# Revit family: LAMP_FIL 70 TECH RECESSED
name_source: partatom
category: Luminarias
revit_build: Autodesk Revit 2015 (Build: 20140606_1530(x64)
units: mm (PartAtom-declared; Revit-internal decimal feet)

## types (16) — shared parameters
CRI = 80
Cambio de temperatura de color de luz atenuada = <Ninguno>
Comentarios de tipo = Availability of switching between accessories through visibility parameters when placed in a project.
Fabricante = LAMP
Filtro de color = 16777215
Gear = Electronic
IEE = A+
IFC Clasificación = Light Fixture
Installation instructions = https://www.lamp.es
Insulation class = I
LED Lifetime = 50.000 L80 B10
Last update = 17/08/2020
Luminaire type = Indoor - Modular System
Lámpara = LED MID-POWER
MacAdam = 3
Manufacturer URL = http://www.lamp.es
Manufacturer country = Spain
Manufacturer name = LAMP
Material Reflector = LAMP_PC Reflector Fil Tech Metalizado
Model explanation = Availability of switching between accessories through visibility parameters when placed in a project.
Product URL = https://www.lamp.es
Product datasheet = https://www.lamp.es
Protection rating = IP20
Type = MID POWER NICHIA
UGR = 19
Ángulo de inclinación = 90,00°

## per-type parameters (varying)
| type | Archivo de red fotométrica | Descripción | Dimensions | Efficacy | Finish | Longitud | Longitud de línea de emisión | Material Perfil | Modelo | Plum | Power | Power Supply | Product code | Recessed dimensions | UniClass 1.4 Code | UniClass 2.0 Code | Weight |
| 1000MM 1600LM 3000K WHITE | 4741120.IES | FIL 70 TECH REC 1M 1600 WW WH. | 1000 x 70 x 70 mm | 106 lm/W | Matt white | 1000 mm  [stored 3.28084 ft] | 1000 mm  [stored 3.28084 ft] | LAMP_Aluminio Perfil Fil BL | F71RE100LOTS830NW | 15 W | 12 W | 230V-50Hz | F71RE100LOTS830NW | 1012 x 78 x 85 mm | F71RE100LOTS830NW | F71RE100LOTS830NW | 2,12 kg |
| 1000MM 1600LM 3000K GREY | 4741123.IES | FIL 70 TECH REC 1M 1600 WW GR. | 1000 x 70 x 70 mm | 106 lm/W | Gloss grey | 1000 mm  [stored 3.28084 ft] | 1000 mm  [stored 3.28084 ft] | LAMP_Aluminio Perfil Fil GR | F71RE100LOTS830NG | 15 W | 12 W | 230V-50Hz | F71RE100LOTS830NG | 1012 x 78 x 85 mm | F71RE100LOTS830NG | F71RE100LOTS830NG | 2,12 kg |
| 1000MM 1600LM 4000K WHITE | 4740120.IES | FIL 70 TECH REC 1M 1600 NW WH. | 1000 x 70 x 70 mm | 106 lm/W | Matt white | 1000 mm  [stored 3.28084 ft] | 1000 mm  [stored 3.28084 ft] | LAMP_Aluminio Perfil Fil BL | F71RE100LOTS840NW | 15 W | 12 W | 220-240V 50-60Hz | F71RE100LOTS840NW | 1012 x 78 x 85 mm | F71RE100LOTS840NW | F71RE100LOTS840NW | 2,12 kg |
| 1000MM 1600LM 4000K GREY | 4740123.IES | FIL 70 TECH REC 1M 1600 NW GR. | 1000 x 70 x 70 mm | 106 lm/W | Gloss grey | 1000 mm  [stored 3.28084 ft] | 1000 mm  [stored 3.28084 ft] | LAMP_Aluminio Perfil Fil GR | F71RE100LOTS840NG | 15 W | 12 W | 220-240V 50-60Hz | F71RE100LOTS840NG | 1012 x 78 x 85 mm | F71RE100LOTS840NG | F71RE100LOTS840NG | 2,12 kg |
| 1000MM 3200LM 3000K WHITE | 4741130.IES | FIL 70 TECH REC 1M 3200 WW WH. | 1000 x 70 x 70 mm | 102 lm/W | Matt white | 1000 mm  [stored 3.28084 ft] | 1000 mm  [stored 3.28084 ft] | LAMP_Aluminio Perfil Fil BL | F71RE100MOTS830NW | 24 W | 21 W | 230V-50Hz | F71RE100MOTS830NW | 1012 x 78 x 85 mm | F71RE100MOTS830NW | F71RE100MOTS830NW | 2,12 kg |
| 1000MM 3200LM 3000K GREY | 4741133.IES | FIL 70 TECH REC 1M 3200 WW GR. | 1000 x 70 x 70 mm | 102 lm/W | Gloss grey | 1000 mm  [stored 3.28084 ft] | 1000 mm  [stored 3.28084 ft] | LAMP_Aluminio Perfil Fil GR | F71RE100MOTS830NG | 24 W | 21 W | 230V-50Hz | F71RE100MOTS830NG | 1012 x 78 x 85 mm | F71RE100MOTS830NG | F71RE100MOTS830NG | 2,12 kg |
| 1000MM 3200LM 4000K WHITE | 4740130.IES | FIL 70 TECH REC 1M 3200 NW WH. | 1000 x 70 x 70 mm | 102 lm/W | Matt white | 1000 mm  [stored 3.28084 ft] | 1000 mm  [stored 3.28084 ft] | LAMP_Aluminio Perfil Fil BL | F71RE100MOTS840NW | 24 W | 21 W | 220-240V 50-60Hz | F71RE100MOTS840NW | 1012 x 78 x 85 mm | F71RE100MOTS840NW | F71RE100MOTS840NW | 2,12 kg |
| 1000MM 3200LM 4000K GREY | 4740133.IES | FIL 70 TECH REC 1M 3200 NW GR. | 1000 x 70 x 70 mm | 102 lm/W | Gloss grey | 1000 mm  [stored 3.28084 ft] | 1000 mm  [stored 3.28084 ft] | LAMP_Aluminio Perfil Fil GR | F71RE100MOTS840NG | 24 W | 21 W | 220-240V 50-60Hz | F71RE100MOTS840NG | 1012 x 78 x 85 mm | F71RE100MOTS840NG | F71RE100MOTS840NG | 2,12 kg |
| 2000MM 3200LM 3000K WHITE | 4741220.IES | FIL 70 TECH REC 2M 3200 WW WH. | 2000 x 70 x 70 mm | 114 lm/W | Matt white | 2000 mm  [stored 6.56168 ft] | 2000 mm  [stored 6.56168 ft] | LAMP_Aluminio Perfil Fil BL | F71RE200MOTS830NW | 27 W | 25 W | 230V-50Hz | F71RE200MOTS830NW | 2012 x 78 x 85 mm | F71RE200MOTS830NW | F71RE200MOTS830NW | 4,25 kg |
| 2000MM 3200LM 3000K GREY | 4741223.IES | FIL 70 TECH REC 2M 3200 WW GR. | 2000 x 70 x 70 mm | 114 lm/W | Gloss grey | 2000 mm  [stored 6.56168 ft] | 2000 mm  [stored 6.56168 ft] | LAMP_Aluminio Perfil Fil GR | F71RE200MOTS830NG | 27 W | 25 W | 230V-50Hz | F71RE200MOTS830NG | 2012 x 78 x 85 mm | F71RE200MOTS830NG | F71RE200MOTS830NG | 4,25 kg |
| 2000MM 3200LM 4000K WHITE | 4740220.IES | FIL 70 TECH REC 2M 3200 NW WH. | 2000 x 70 x 70 mm | 114 lm/W | Matt white | 2000 mm  [stored 6.56168 ft] | 2000 mm  [stored 6.56168 ft] | LAMP_Aluminio Perfil Fil BL | F71RE200MOTS840NW | 27 W | 25 W | 220-240V 50-60Hz | F71RE200MOTS840NW | 2012 x 78 x 85 mm | F71RE200MOTS840NW | F71RE200MOTS840NW | 4,25 kg |
| 2000MM 3200LM 4000K GREY | 4740223.IES | FIL 70 TECH REC 2M 3200 NW GR. | 2000 x 70 x 70 mm | 135 lm/W | Gloss grey | 2000 mm  [stored 6.56168 ft] | 2000 mm  [stored 6.56168 ft] | LAMP_Aluminio Perfil Fil GR | F71RE200MOTS840NG | 27 W | 25 W | 220-240V 50-60Hz | F71RE200MOTS840NG | 2012 x 78 x 85 mm | F71RE200MOTS840NG | F71RE200MOTS840NG | 4,25 kg |
| 2000MM 6400LM 3000K WHITE | 4741230.IES | FIL 70 TECH REC 2M 6400 WW WH. | 2000 x 70 x 70 mm | 129 lm/W | Matt white | 2000 mm  [stored 6.56168 ft] | 2000 mm  [stored 6.56168 ft] | LAMP_Aluminio Perfil Fil BL | F71RE200HOTS830NW | 45 W | 42 W | 230V-50Hz | F71RE200HOTS830NW | 2012 x 78 x 85 mm | F71RE200HOTS830NW | F71RE200HOTS830NW | 4,25 kg |
| 2000MM 6400LM 3000K GREY | 4741233.IES | FIL 70 TECH REC 2M 6400 WW GR. | 2000 x 70 x 70 mm | 107 lm/W | Gloss grey | 2000 mm  [stored 6.56168 ft] | 2000 mm  [stored 6.56168 ft] | LAMP_Aluminio Perfil Fil GR | F71RE200HOTS830NG | 45 W | 42 W | 230V-50Hz | F71RE200HOTS830NG | 2012 x 78 x 85 mm | F71RE200HOTS830NG | F71RE200HOTS830NG | 4,25 kg |
| 2000MM 6400LM 4000K WHITE | 4740230.IES | FIL 70 TECH REC 2M 6400 NW WH. | 2000 x 70 x 70 mm | 129 lm/W | Matt white | 2000 mm  [stored 6.56168 ft] | 2000 mm  [stored 6.56168 ft] | LAMP_Aluminio Perfil Fil BL | F71RE200HOTS840NW | 45 W | 42 W | 220-240V 50-60Hz | F71RE200HOTS840NW | 2012 x 78 x 85 mm | F71RE200HOTS840NW | F71RE200HOTS840NW | 4,25 kg |
| 2000MM 6400LM 4000K GREY | 4740233.IES | FIL 70 TECH REC 2M 6400 NW GR. | 2000 x 70 x 70 mm | 107 lm/W | Gloss grey | 2000 mm  [stored 6.56168 ft] | 2000 mm  [stored 6.56168 ft] | LAMP_Aluminio Perfil Fil GR | F71RE200HOTS840NG | 45 W | 42 W | 220-240V 50-60Hz | F71RE200HOTS840NG | 2012 x 78 x 85 mm | F71RE200HOTS840NG | F71RE200HOTS840NG | 4,25 kg |

note: [stored X ft] marks values corroborated as IEEE doubles in the binary element streams (Revit-internal decimal feet)

## geometry (parser evidence)
native form markers: Blend x10
no freeform markers — native parametric forms only
